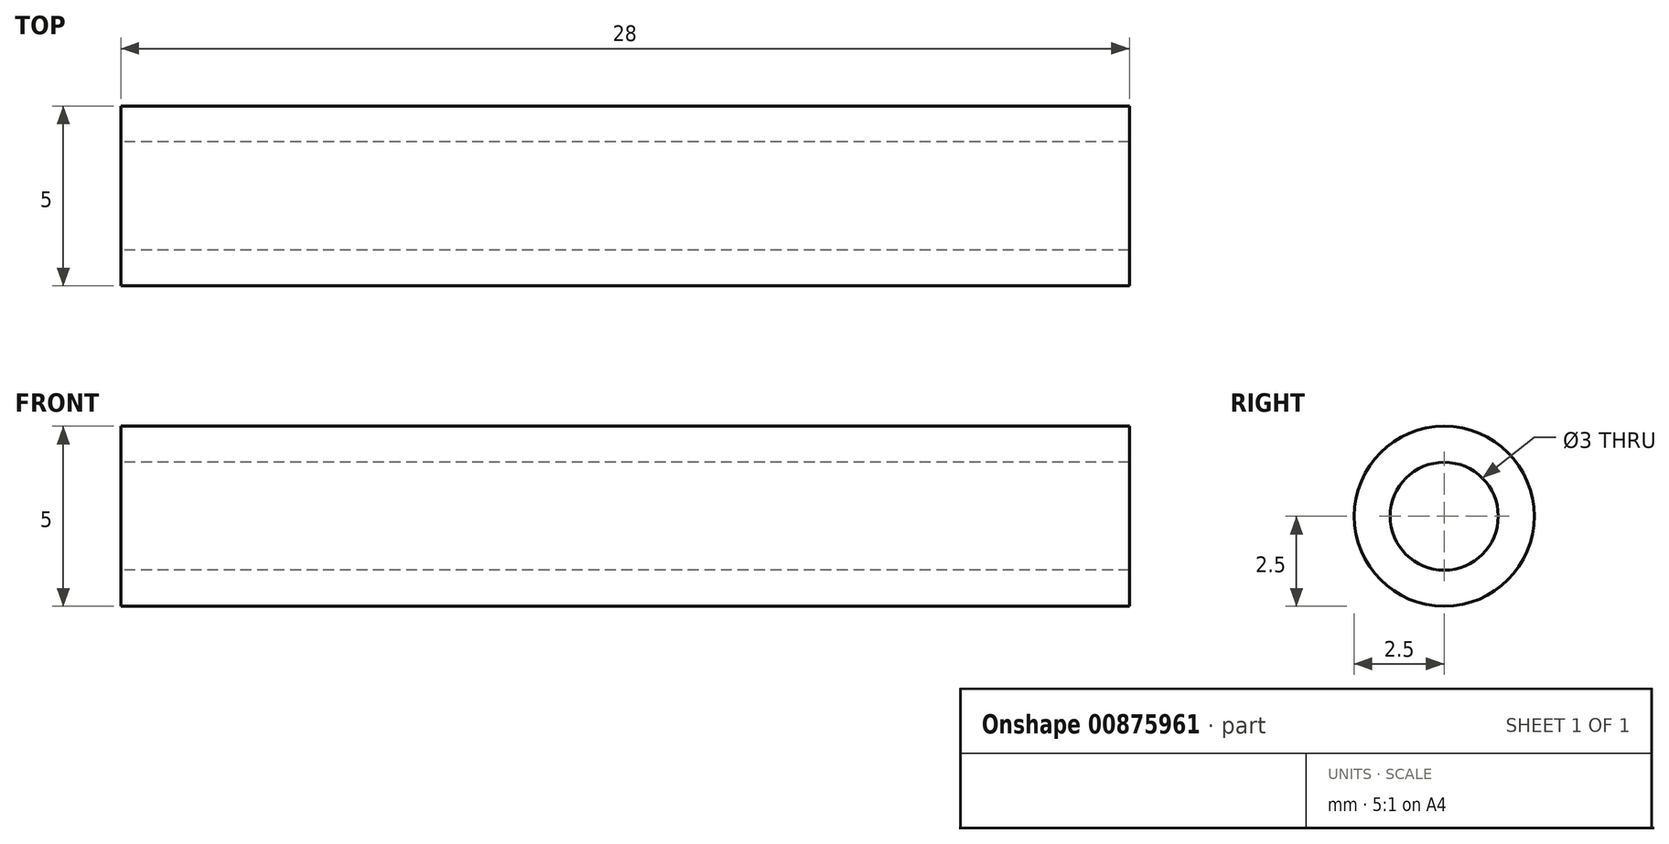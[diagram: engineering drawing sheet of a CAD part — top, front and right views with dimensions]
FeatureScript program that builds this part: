
annotation { "Feature Type Name" : "Feature", "Feature Type Description" : "" }
export const myFeature = defineFeature(function(context is Context, id is Id, definition is map)
    precondition{}
    {
        {
            var Q0;
            Q0=qCreatedBy(makeId("Right.planeOp"),FACE);
            var sketch = newSketch(context, id + "F0", { "sketchPlane" : qUnion([Q0])});
            skCircle(sketch, "E0", {"center": v(0, 0) * mm, "radius": 2.5 * mm});
            skCircle(sketch, "E1", {"center": v(0, 0) * mm, "radius": 1.5 * mm});
            skSolve(sketch);
        }
        {
            var Q0;
            Q0=qSketchRegion(id+"F0",true);
            extrude(context, id + "F1", {"entities" : qUnion([Q0]), "endBound" : BoundingType.SYMMETRIC, "depth" : 28 * mm, "offsetDistance" : 25 * mm});
        }
    });
